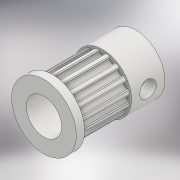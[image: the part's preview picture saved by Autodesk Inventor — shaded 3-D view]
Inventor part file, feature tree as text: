
AUTODESK INVENTOR PART (.ipt)
format: ipt  version: 2018.2 (Build 222227000, 227)  size: 257,536 bytes
history: native  units: mm
features: extrude x6, sketch x5, pattern_circular x1
ambient origin geometry x8: Origin, YZ Plane, XZ Plane, XY Plane, X Axis, Y Axis, Z Axis, Center Point
bodies: Solid1 (feature_tree)
feature tree (12):
  extrude  "Extrusion1"  Depth=0.5mm
  extrude  "Extrusion2"  Depth=7.0mm TaperAngle=0.0deg
  pattern_circular  "Circular Pattern1"  [2 undecoded]
  extrude  "Extrusion3"  Depth=1.0mm TaperAngle=0.0deg
  sketch  "Sketch4"  dims[d18=6.35mm]
  extrude  "Extrusion4"  Depth=6.0mm TaperAngle=0.0deg
  extrude  "Extrusion5"  Depth=3.0mm
  extrude  "Extrusion6"  Depth=6.0mm TaperAngle=0.0deg
  sketch  "Sketch1"  dims[d8=0.0mm d9=0.5mm]
  sketch  "Sketch2"  dims[d10=0.15mm d12=7.0mm d13=0.0mm]
  sketch  "Sketch3"  dims[d15=360.0deg]
  sketch  "Sketch5"  dims[d20=0.0mm d21=2.0mm d22=1.0mm d23=0.0mm d24=6.0mm d25=0.0mm d26=3.0mm d27=6.0mm d28=0.0mm]
note: 2 required parameter values undecoded (feature->parameter linkage not recoverable at this tier; creation-order binding heuristic only, values carry confidence <= 0.55)
